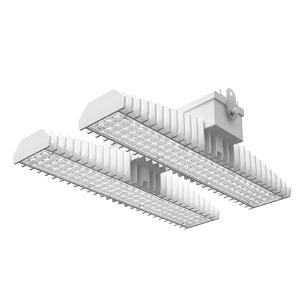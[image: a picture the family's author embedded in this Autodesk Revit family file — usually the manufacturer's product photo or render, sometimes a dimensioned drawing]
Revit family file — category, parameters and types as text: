
# Revit family: 3f_filippi_-_3f_lem_concentrato_3f_filippi_-_59164_a0811_-_3f_lem_2_led_100-865_cr_conc___vt_e534
name_source: partatom
category: Lighting Fixtures
units: mm (PartAtom-declared; Revit-internal decimal feet)

## family parameters
Cut with Voids When Loaded = No
Host = Face
Light Source = No
Part Type = Normal
Room Calculation Point = No
Round Connector Dimension = Use Diameter
Shared = No

## types (1)
- 3F Filippi - 3F LEM Concentrato (1 x LED, 15155 lm, 109 W, 6500 K)
    Apparent Load = 109 VA
    Approval mark = CE
    CIE Flux Codes = 83 96 99 100 100
    Color Rendering = 80
    Color Temperature = 6500 K
    Control Gear = Electronic ballast
    Default Elevation = 1800 mm
    Description = Industrial luminaire with high light output and high luminous efficiency designed with the most innovative technologies for environments with temperature up to 55°C.

ILLUMINOTECHNICAL
Luminous efficiency 100% (DLOR 99%, ULOR 1%).
Initial luminous flux of the luminaire 15155 lm.
Direct symmetric narrow distribution: the illuminated area has a elliptical shape.
Installation Interdistance Transv.D = 0.52 x hu - Long.D = 1.16 x hu.
Tabular UGR (CIE 117 - 4H-8H; S=0.25H; 70/50/20): RUG 16.4 - 20.3.
Beam angle: 31° - 73°.
Luminous efficacy 139 lm/W.
Lifetime (L93/B10): 30000 h. (tq+25°C)
Lifetime (L90/B10): 50000 h. (tq+25°C)
Lifetime (L85/B10): 80000 h. (tq+25°C)
Lifetime (L80/B10): 100000 h. (tq+25°C)
Lifetime (L85/B10): 50000 h. (tq+55°C)
Sudden decreased luminous flux after 50000 hours: 0% (C0).
Photobiological safety in compliance with IEC/TR 62778: RG0 risk exempt, (IEC 62471).
In compliance with IEC/EN 62722-2-1 - IEC/EN 62717 standards.

SOURCE
2 Mid-Power linear LED modules 50W/865.
Energy efficiency class (UE 2019/2020 - UE 2019/2015): C.
CIE 13.3 Colour rendering index: CRI >80 (R9 <50%).
IES TM-30 Fidelity Index: Rf = 84 Rg = 95.
CCT nominal colour temperature 6500 K.
Colour initial tolerance (MacAdam): SDCM 3.

MECHANICAL
Passive modular heatsinks in die-casted aluminium, painted in white colour.
To optimize the thermal management of the LED module, the heatsinks are oversized and provided with self-cleaning of cooling fins.
Wiring body in aluminium and galvanised steel anchored solidly to the sinks and thermally separated.
3F Lens lenses with high luminous efficiency, transparent methacrylate (PMMA), fixed to the LED modules.
Fixing brackets in stainless steel.
Luminaire with limited surface temperature. - D - (EN 60598-2-24)
Dimensions: 470x542 mm, height 133 mm. Weight 10.544 kg.
IP65 protection degree.
Mechanical strength to impacts IK06 (1 joule).
Glow-wire test resistance 650°C.

ELECTRICAL
Halogen Free electronic wiring 230V-50/60Hz, power factor 0.97, THD <25%, constant output current, class I, 1 driver.
Power of the luminaire 109 W.
ENEC - CE.
SAFE FLICKER: PstLM=<1 and SVM=<0.4 (IEC TR 61547-1 and IEC TR 63158), to ensure a more comfortable and safe light.
Luminaire compliant with EN 60598-2-22 for power supply from a centralised emergency system CPSS (Central Power Supply System), not incorporated in the luminaire - high risk areas excluded. The default power and flux are 100% in AC and 100% in DC.
Ambient temperature from -30°C to +55°C.
Temperature class T6 max 85°C.
Quick connection via M20 3P connector with 9-13 mm tightening range.
Power unit positioned on a separate compartment by the LED module to ensure optimum temperatures of cabling components, to be inspectable and maintainable.
Relative humidity UR: <85%.

INSTALLATION
Ceiling / Suspended / Wall.
All accessories dedicated to this product are available on the Catalog and on our website www.3F-Filippi.com.

ACCESSORIES
A0811 - VT transparent glass, tempered, not flammable, with sealing gasket.
One required for each light module. The pack contains 10 pieces.

APPLICATIONS
In commercial environments, exhibition and industrial areas, stores, open areas.
Applications with high ambient temperature up to 55°C.
Environments in which it is necessary a total protection against falling fragments (eg environments with foodstuffs or machines with moving parts or with extreme temperature changes), use luminaires with polycarbonate lenses.

WARNING
Fixture not suitable for cold stores with an ambient temperature <0°C and/or relative humidity >85%.
Luminaire designed for disposal/recycling at end-of-life.
Replaceable (LED only) light source by a professional. Replaceable control gear by a professional.
    Height = 133 mm  [stored 0.436352 ft]
    Lamp = 1 x LED
    Lamp Light Flux = 15155 lm
    Lamp Power = 109 W
    Lamp count = 1
    Length = 470 mm
    Lifetime = 50000 h
    Luminous efficacy = 139 lm/W
    Manufacturer = 3F Filippi
    ModVariant = No
    Model = 3F Filippi - 59164+A0811 - 3F LEM 2 LED 100-865 CR CONC + VT
    Mounting Place = Ceiling
    Mounting Type = Pendant
    Number of Poles = 1
    OnlyDefault = Yes
    Power Factor = 1
    Product Name = 3F Filippi - 3F LEM Concentrato
    Product group = pendant luminaire
    ProductGroupID = 9
    Protection Class = Protection class I
    Protection Degree = IP 65
    RLX_Detail_Level = 1
    RLX_Emergency_Light_Flux = 0 lm
    RLX_Emergency_Type = 0
    RLX_Emergency_Type_DB = No
    RlxData = <blob elided: 102773 chars, md5=2128179e>
    Socket = socket
    Standby Power = 0 W
    System Light Flux = 15155 lm
    System Power = 109 W
    Type Comments = Product without accessories
    Type Image = 3f_filippi_-_lem_2__a0811.jpg
    URL = http://relux.com
    VarID = ---
    Voltage = 0 V
    Weight = 0.00 kg
    Width = 542 mm

note: [stored X ft] marks values corroborated as IEEE doubles in the binary element streams (Revit-internal decimal feet)

## geometry (parser evidence)
native form markers: Blend x4, Sweep x11
no freeform markers — native parametric forms only
